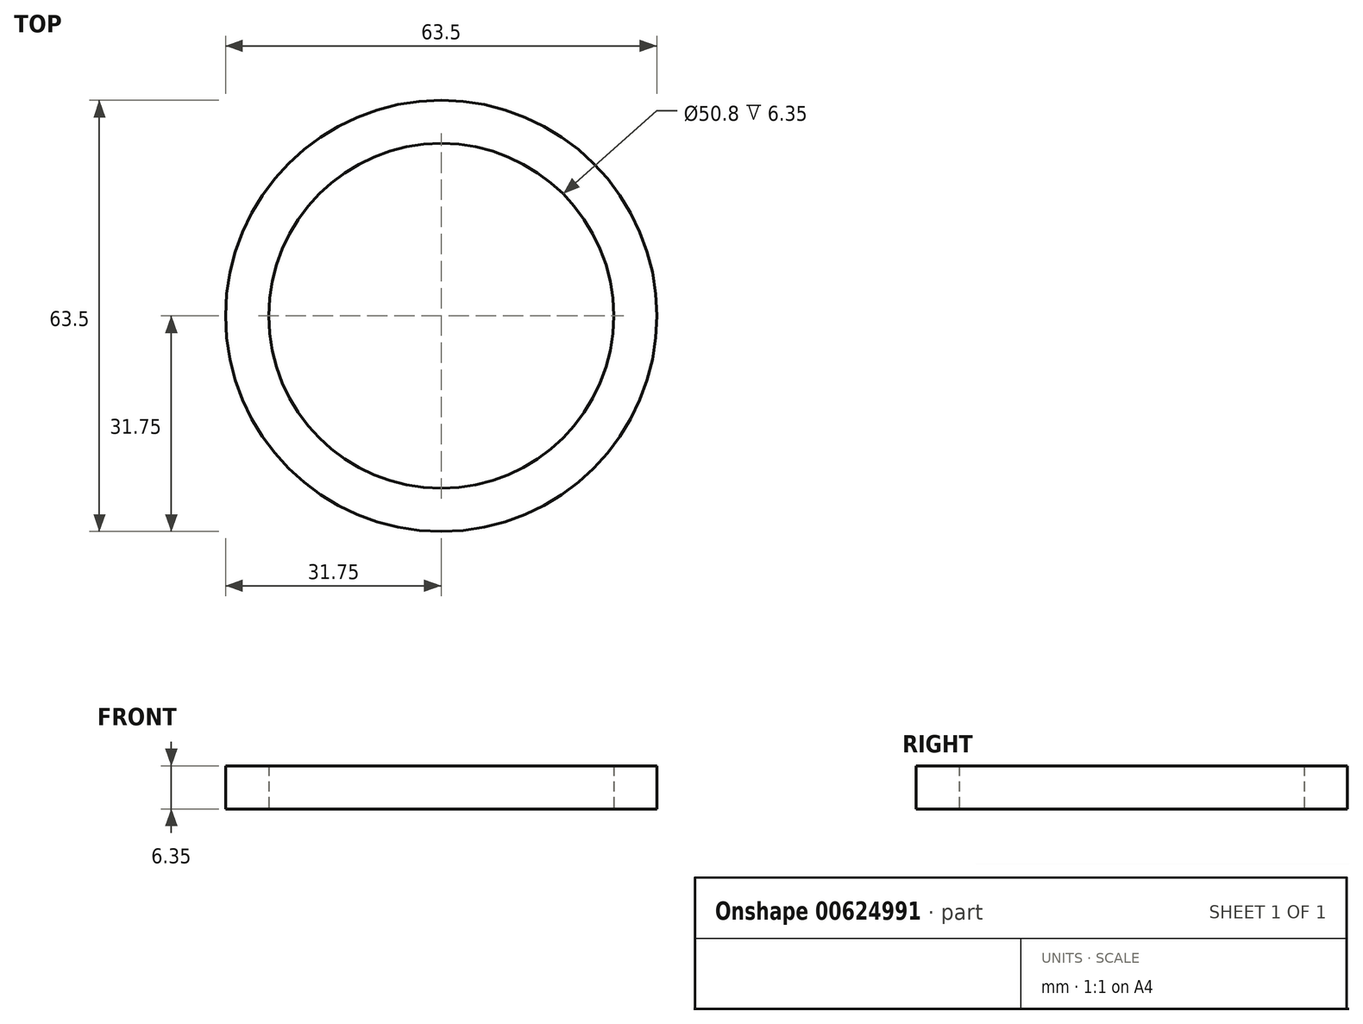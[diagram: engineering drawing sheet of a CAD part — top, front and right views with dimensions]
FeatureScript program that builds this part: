
annotation { "Feature Type Name" : "Feature", "Feature Type Description" : "" }
export const myFeature = defineFeature(function(context is Context, id is Id, definition is map)
    precondition{}
    {
        {
            var Q0;
            Q0=qCreatedBy(makeId("Top.planeOp"),FACE);
            var sketch = newSketch(context, id + "F0", { "sketchPlane" : qUnion([Q0])});
            skCircle(sketch, "E0", {"center": v(0, 0) * mm, "radius": 31.75 * mm});
            skCircle(sketch, "E1", {"center": v(0, 0) * mm, "radius": 25.4 * mm});
            skSolve(sketch);
        }
        {
            var Q0;
            Q0=makeQuery(id+"F0.imprint","IMPRINT",FACE,{"disambiguationData":[TD([[makeQuery(id+"F0.imprint","IMPRINT",EDGE,{"derivedFrom":sQuery(id+"F0.wireOp",EDGE,"E0")}),1.0]])]});
            extrude(context, id + "F1", {"entities" : qUnion([Q0]), "depth" : 6.35 * mm, "offsetDistance" : 25.4 * mm});
        }
    });
